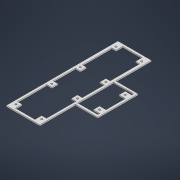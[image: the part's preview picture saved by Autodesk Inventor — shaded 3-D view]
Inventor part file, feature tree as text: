
AUTODESK INVENTOR PART (.ipt)
format: ipt  version: 2021 (Build 250183000, 183)  size: 377,856 bytes
history: native  units: mm
features: extrude x3, sketch x2
ambient origin geometry x8: Origin, YZ Plane, XZ Plane, XY Plane, X Axis, Y Axis, Z Axis, Center Point
bodies: Volumenkörper1 (feature_tree)
feature tree (5):
  extrude  "Extrusion1"  Depth=200.0mm
  extrude  "Extrusion3"  Depth=15.6mm
  extrude  "Extrusion2"  Depth=15.6mm
  sketch  "Skizze1"  dims[d0=60.0mm d1=200.0mm]
  sketch  "Skizze3"  dims[d2=2.0mm d3=0.0mm d4=3.2mm d5=3.2mm d6=10.5mm d7=10.5mm d8=23.0mm d9=23.0mm d10=3.2mm d11=3.2mm d12=23.0mm d13=23.0mm d14=25.5mm d15=25.5mm d16=5.0mm d17=5.0mm d19=4.0mm d20=5.0mm d23=4.0mm d24=4.0mm d25=4.0mm d26=4.0mm d27=4.0mm d28=4.0mm d29=4.0mm d30=4.0mm d31=4.0mm d32=4.0mm d33=4.0mm d34=4.0mm d35=4.0mm d36=4.0mm d37=4.0mm d38=4.0mm d39=4.0mm d40=4.0mm d41=4.0mm d42=4.0mm d43=4.0mm d44=4.0mm d45=4.0mm d48=12.6mm d49=12.6mm d50=12.6mm d51=12.6mm d52=12.6mm d53=12.6mm d54=2.0mm d55=0.0mm d56=40.0mm d57=0.0mm d58=3.2mm d59=3.2mm d60=23.0mm d61=23.0mm d64=37.0mm d65=37.0mm d66=4.0mm d67=4.0mm d68=4.0mm d69=4.0mm d70=4.0mm d71=4.0mm d72=4.0mm d73=4.0mm d74=4.0mm d75=4.0mm d76=4.0mm d77=15.6mm d78=15.6mm]
